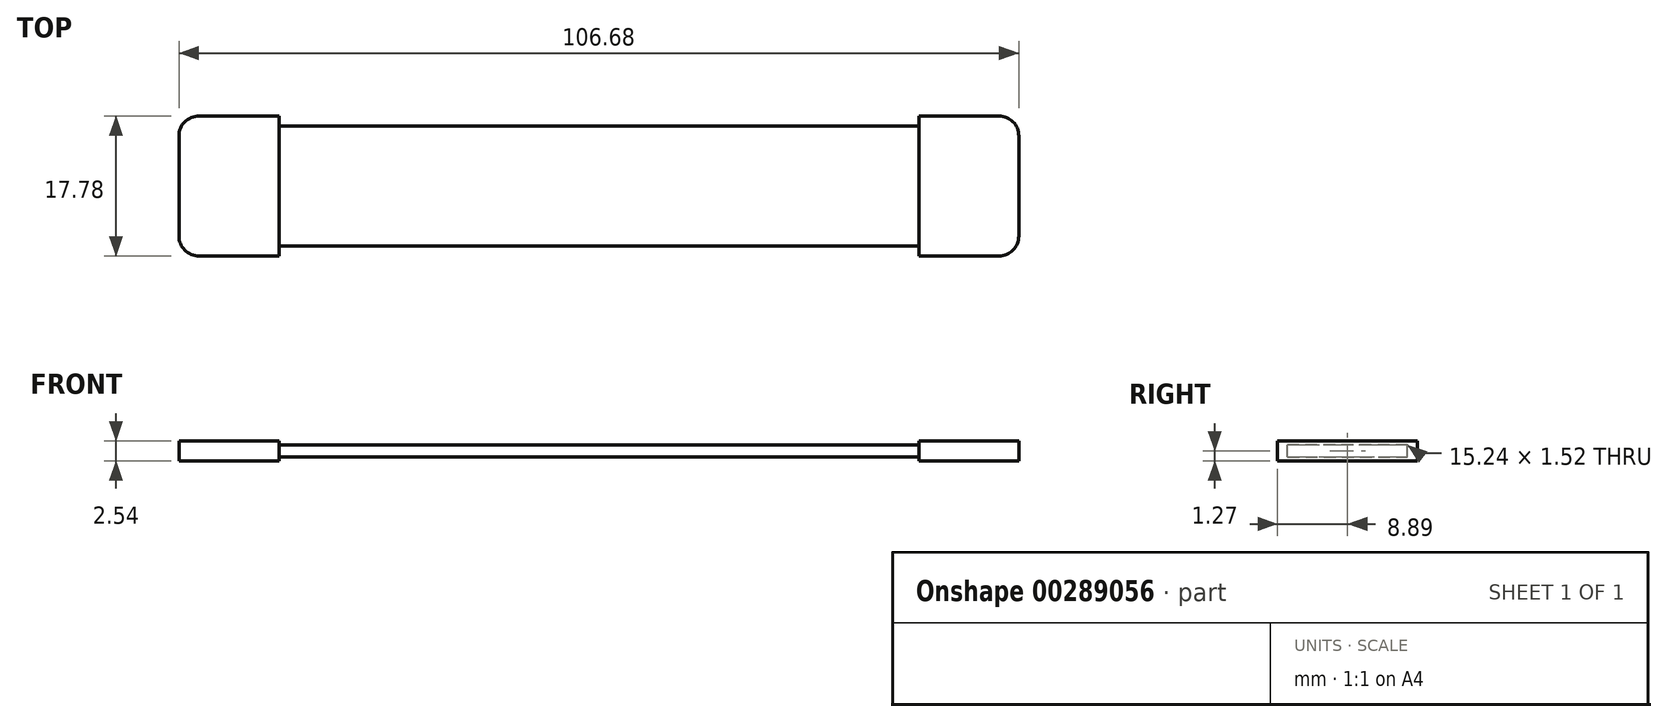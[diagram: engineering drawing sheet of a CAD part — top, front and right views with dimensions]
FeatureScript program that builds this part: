
annotation { "Feature Type Name" : "Feature", "Feature Type Description" : "" }
export const myFeature = defineFeature(function(context is Context, id is Id, definition is map)
    precondition{}
    {
        {
            var Q0;
            Q0=qCreatedBy(makeId("Top.planeOp"),FACE);
            var sketch = newSketch(context, id + "F0", { "sketchPlane" : qUnion([Q0])});
            skLineSegment(sketch, "E0.bottom", {"start": v(0, 0) * mm, "end": v(106.68, 0) * mm});
            skLineSegment(sketch, "E0.top", {"start": v(0, 17.78) * mm, "end": v(106.68, 17.78) * mm});
            skLineSegment(sketch, "E0.left", {"start": v(0, 0) * mm, "end": v(0, 17.78) * mm});
            skLineSegment(sketch, "E0.right", {"start": v(106.68, 0) * mm, "end": v(106.68, 17.78) * mm});
            skSolve(sketch);
        }
        {
            var Q0;
            Q0=makeQuery(id+"F0.imprint","IMPRINT",FACE,{"disambiguationData":[TD([[makeQuery(id+"F0.imprint","IMPRINT",EDGE,{"derivedFrom":sQuery(id+"F0.wireOp",EDGE,"E0.bottom")}),1.0]])]});
            extrude(context, id + "F1", {"entities" : qUnion([Q0]), "depth" : 2.54 * mm});
        }
        {
            var Q0;
            Q0=makeQuery(id+"F1.opExtrude","SWEPT_EDGE",EDGE,{"disambiguationData":[OSD([sQuery(id+"F0.wireOp",EDGE,"E0.top"),sQuery(id+"F0.wireOp",EDGE,"E0.right")])]});
            var Q1;
            Q1=makeQuery(id+"F1.opExtrude","SWEPT_EDGE",EDGE,{"disambiguationData":[OSD([sQuery(id+"F0.wireOp",EDGE,"E0.bottom"),sQuery(id+"F0.wireOp",EDGE,"E0.right")])]});
            var Q2;
            Q2=makeQuery(id+"F1.opExtrude","SWEPT_EDGE",EDGE,{"disambiguationData":[OSD([sQuery(id+"F0.wireOp",EDGE,"E0.top"),sQuery(id+"F0.wireOp",EDGE,"E0.left")])]});
            var Q3;
            Q3=makeQuery(id+"F1.opExtrude","SWEPT_EDGE",EDGE,{"disambiguationData":[OSD([sQuery(id+"F0.wireOp",EDGE,"E0.bottom"),sQuery(id+"F0.wireOp",EDGE,"E0.left")])]});
            fillet(context, id + "F2", {"entities" : qUnion([Q0, Q1, Q2, Q3]), "radius" : 2.54 * mm, "tangentPropagation" : true, "allowEdgeOverflow" : false});
        }
        {
            var Q0;
            Q0=makeQuery(id+"F1.opExtrude","CAP_FACE",FACE,{"disambiguationData":[OSD([sQuery(id+"F0.wireOp",EDGE,"E0.bottom"),sQuery(id+"F0.wireOp",EDGE,"E0.top"),sQuery(id+"F0.wireOp",EDGE,"E0.left"),sQuery(id+"F0.wireOp",EDGE,"E0.right")])],"isStart":false});
            var sketch = newSketch(context, id + "F3", { "sketchPlane" : qUnion([Q0])});
            skLineSegment(sketch, "E1.bottom", {"start": v(12.7, 17.78) * mm, "end": v(93.98, 17.78) * mm});
            skLineSegment(sketch, "E1.top", {"start": v(12.7, 16.51) * mm, "end": v(93.98, 16.51) * mm});
            skLineSegment(sketch, "E1.left", {"start": v(12.7, 17.78) * mm, "end": v(12.7, 16.51) * mm});
            skLineSegment(sketch, "E1.right", {"start": v(93.98, 17.78) * mm, "end": v(93.98, 16.51) * mm});
            skLineSegment(sketch, "E2.bottom", {"start": v(12.7, 0) * mm, "end": v(93.98, 0) * mm});
            skLineSegment(sketch, "E2.top", {"start": v(12.7, 1.27) * mm, "end": v(93.98, 1.27) * mm});
            skLineSegment(sketch, "E2.left", {"start": v(12.7, 0) * mm, "end": v(12.7, 1.27) * mm});
            skLineSegment(sketch, "E2.right", {"start": v(93.98, 0) * mm, "end": v(93.98, 1.27) * mm});
            skSolve(sketch);
        }
        {
            var Q0;
            Q0 = qSketchRegion(id + "F3", true);
            extrude(context, id + "F4", {"entities" : qUnion([Q0]), "operationType" : NewBodyOperationType.REMOVE, "oppositeDirection" : true, "depth" : 25.4 * mm});
        }
        {
            var Q0;
            Q0=makeQuery(id+"F1.opExtrude","CAP_FACE",FACE,{"disambiguationData":[OSD([sQuery(id+"F0.wireOp",EDGE,"E0.bottom"),sQuery(id+"F0.wireOp",EDGE,"E0.top"),sQuery(id+"F0.wireOp",EDGE,"E0.left"),sQuery(id+"F0.wireOp",EDGE,"E0.right")])],"isStart":false});
            var sketch = newSketch(context, id + "F5", { "sketchPlane" : qUnion([Q0])});
            skLineSegment(sketch, "E3.bottom", {"start": v(12.7, 16.51) * mm, "end": v(93.98, 16.51) * mm});
            skLineSegment(sketch, "E3.top", {"start": v(12.7, 1.27) * mm, "end": v(93.98, 1.27) * mm});
            skLineSegment(sketch, "E3.left", {"start": v(12.7, 16.51) * mm, "end": v(12.7, 1.27) * mm});
            skLineSegment(sketch, "E3.right", {"start": v(93.98, 16.51) * mm, "end": v(93.98, 1.27) * mm});
            skSolve(sketch);
        }
        {
            var Q0;
            Q0 = qSketchRegion(id + "F5", true);
            extrude(context, id + "F6", {"entities" : qUnion([Q0]), "operationType" : NewBodyOperationType.REMOVE, "oppositeDirection" : true, "depth" : 0.5 * mm});
        }
        {
            var Q0;
            Q0=makeQuery(id+"F1.opExtrude","CAP_FACE",FACE,{"disambiguationData":[OSD([sQuery(id+"F0.wireOp",EDGE,"E0.bottom"),sQuery(id+"F0.wireOp",EDGE,"E0.top"),sQuery(id+"F0.wireOp",EDGE,"E0.left"),sQuery(id+"F0.wireOp",EDGE,"E0.right")])],"isStart":true});
            var sketch = newSketch(context, id + "F7", { "sketchPlane" : qUnion([Q0])});
            skLineSegment(sketch, "E4.bottom", {"start": v(12.7, 0) * mm, "end": v(93.98, 0) * mm});
            skLineSegment(sketch, "E4.top", {"start": v(12.7, -16.51) * mm, "end": v(93.98, -16.51) * mm});
            skLineSegment(sketch, "E4.left", {"start": v(12.7, 0) * mm, "end": v(12.7, -16.51) * mm});
            skLineSegment(sketch, "E4.right", {"start": v(93.98, 0) * mm, "end": v(93.98, -16.51) * mm});
            skSolve(sketch);
        }
        {
            var Q0;
            Q0 = qSketchRegion(id + "F7", true);
            extrude(context, id + "F8", {"entities" : qUnion([Q0]), "operationType" : NewBodyOperationType.REMOVE, "oppositeDirection" : true, "depth" : 0.5 * mm});
        }
    });
